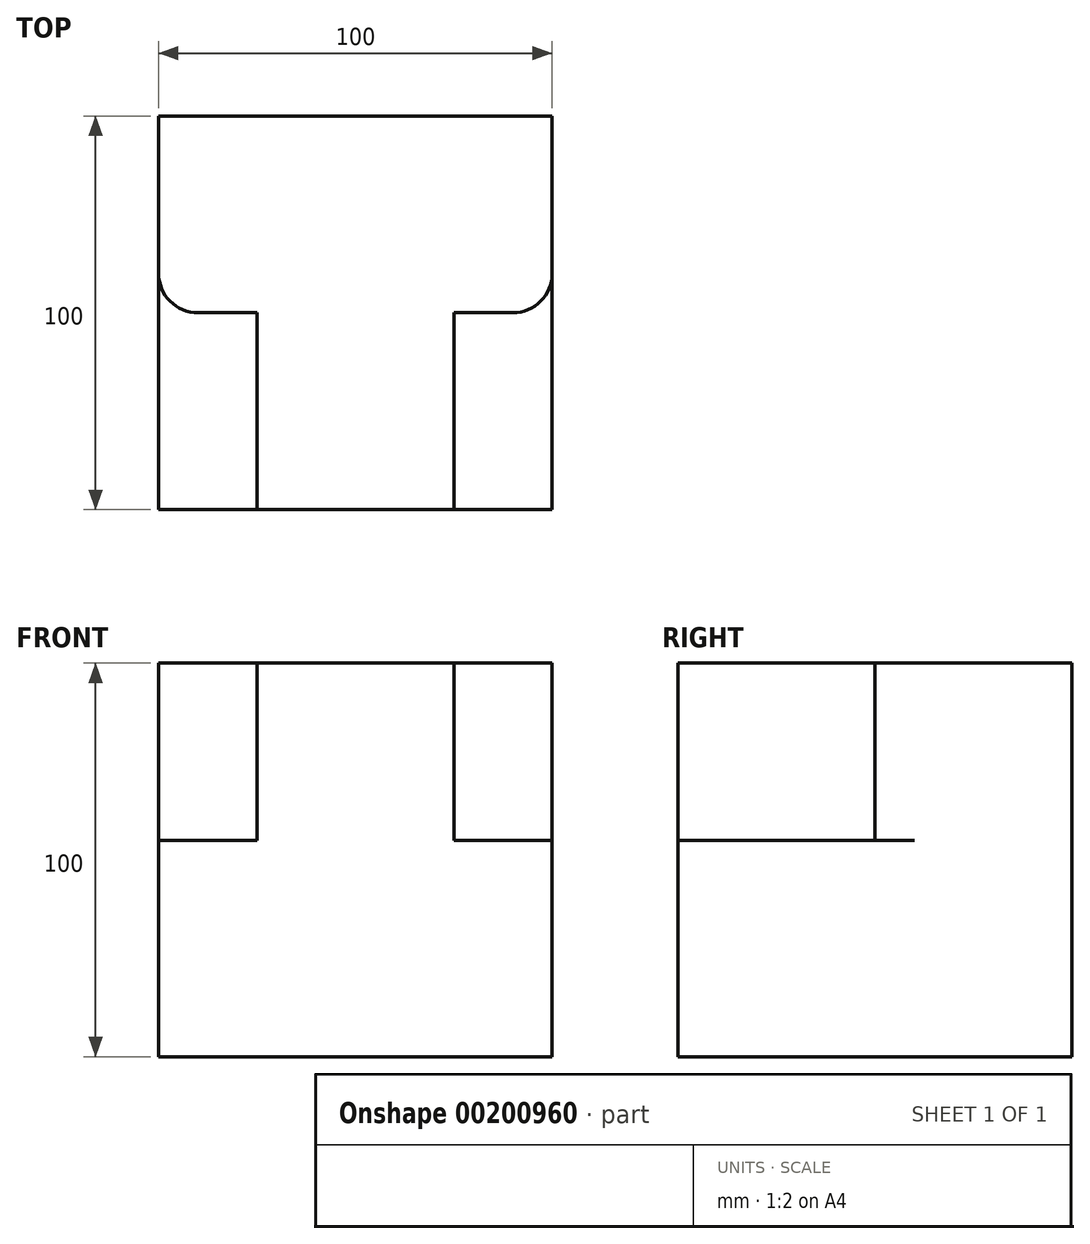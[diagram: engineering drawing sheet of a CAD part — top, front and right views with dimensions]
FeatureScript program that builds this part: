
annotation { "Feature Type Name" : "Feature", "Feature Type Description" : "" }
export const myFeature = defineFeature(function(context is Context, id is Id, definition is map)
    precondition{}
    {
        {
            var Q0;
            Q0=qCreatedBy(makeId("Right.planeOp"),FACE);
            var sketch = newSketch(context, id + "F0", { "sketchPlane" : qUnion([Q0])});
            skLineSegment(sketch, "E0", {"start": v(0, 0) * mm, "end": v(100, 0) * mm});
            skLineSegment(sketch, "E1", {"start": v(100, 0) * mm, "end": v(100, 100) * mm});
            skLineSegment(sketch, "E2", {"start": v(100, 100) * mm, "end": v(0, 100) * mm});
            skLineSegment(sketch, "E3", {"start": v(0, 100) * mm, "end": v(0, 0) * mm});
            skSolve(sketch);
        }
        {
            var Q0;
            Q0=makeQuery(id+"F0.imprint","IMPRINT",FACE,{"disambiguationData":[TD([[makeQuery(id+"F0.imprint","IMPRINT",EDGE,{"derivedFrom":sQuery(id+"F0.wireOp",EDGE,"E0")}),1.0]])]});
            extrude(context, id + "F1", {"entities" : qUnion([Q0]), "depth" : 100 * mm});
        }
        {
            var Q0;
            Q0=makeQuery(id+"F1.opExtrude","SWEPT_FACE",FACE,{"disambiguationData":[OSD([sQuery(id+"F0.wireOp",EDGE,"E2")])]});
            var sketch = newSketch(context, id + "F2", { "sketchPlane" : qUnion([Q0])});
            skLineSegment(sketch, "E4", {"start": v(0, 100) * mm, "end": v(0, 60) * mm});
            skLineSegment(sketch, "E5", {"start": v(10, 50) * mm, "end": v(25, 50) * mm});
            skLineSegment(sketch, "E6", {"start": v(25, 50) * mm, "end": v(25, 0) * mm});
            skLineSegment(sketch, "E7", {"start": v(25, 0) * mm, "end": v(75, 0) * mm});
            skLineSegment(sketch, "E8", {"start": v(75, 0) * mm, "end": v(75, 50) * mm});
            skLineSegment(sketch, "E9", {"start": v(99.54, 100.08) * mm, "end": v(0, 100) * mm});
            skPoint(sketch, "E10.visualSharp", {"position": v(0, 50) * mm});
            skArc(sketch, "E10.filletArc", {"start": v(0, 60) * mm, "mid": v(2.93, 52.93) * mm, "end": v(10, 50) * mm});
            skPoint(sketch, "E11.visualSharp", {"position": v(100, 50) * mm});
            skLineSegment(sketch, "E12", {"start": v(75, 50) * mm, "end": v(90, 50) * mm});
            skLineSegment(sketch, "E13", {"start": v(100, 60) * mm, "end": v(100, 100) * mm});
            skArc(sketch, "E14.filletArc", {"start": v(90, 50) * mm, "mid": v(97.07, 52.93) * mm, "end": v(100, 60) * mm});
            skSolve(sketch);
        }
        {
            var Q0;
            Q0=makeQuery(id+"F2.imprint","IMPRINT",FACE,{"disambiguationData":[TD([[makeQuery(id+"F2.imprint","IMPRINT",EDGE,{"derivedFrom":sQuery(id+"F2.wireOp",EDGE,"E5")}),-1.0]])]});
            var Q1;
            {var subQ5=sQuery(id+"F2.wireOp",EDGE,"E8");Q1=makeQuery(id+"F2.imprint","IMPRINT",FACE,{"disambiguationData":[TD([[makeQuery(id+"F2.imprint","IMPRINT",EDGE,{"derivedFrom":subQ5}),-1.0]])]});}
            extrude(context, id + "F3", {"entities" : qUnion([Q0, Q1]), "operationType" : NewBodyOperationType.REMOVE, "oppositeDirection" : true, "depth" : 45 * mm});
        }
    });
